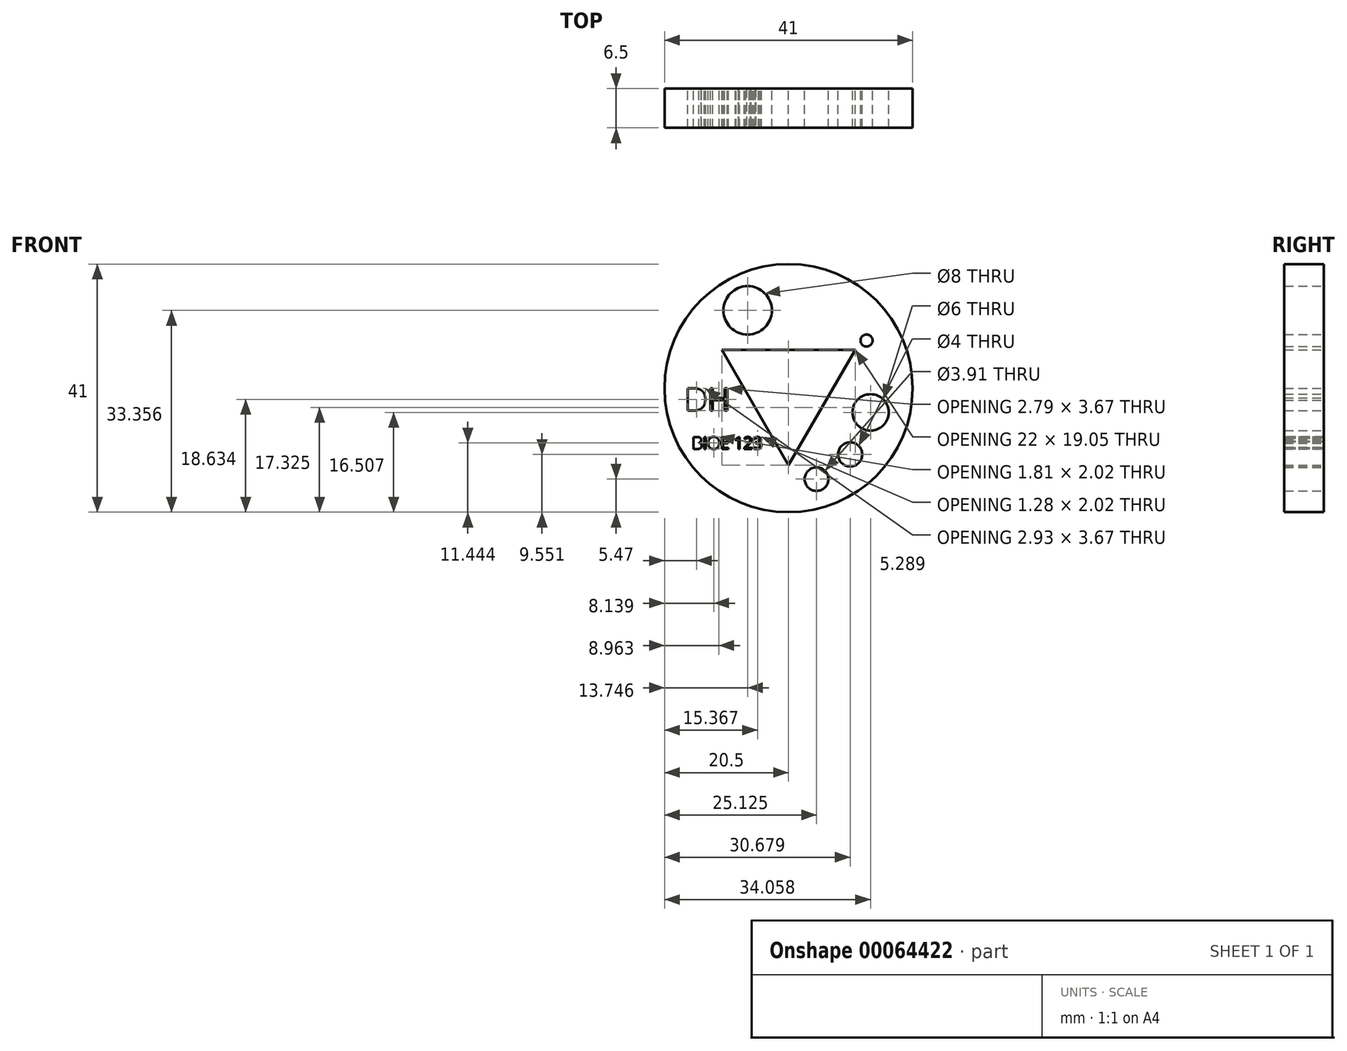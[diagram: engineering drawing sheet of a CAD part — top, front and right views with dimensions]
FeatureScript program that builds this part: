
annotation { "Feature Type Name" : "Feature", "Feature Type Description" : "" }
export const myFeature = defineFeature(function(context is Context, id is Id, definition is map)
    precondition{}
    {
        {
            var Q0;
            Q0=qCreatedBy(makeId("Front.planeOp"),FACE);
            var sketch = newSketch(context, id + "F0", { "sketchPlane" : qUnion([Q0])});
            skCircle(sketch, "E0", {"center": v(0, 0) * mm, "radius": 27.5 * mm});
            skCircle(sketch, "E1", {"center": v(0, 0) * mm, "radius": 20.5 * mm});
            skCircle(sketch, "E2", {"center": v(-6.75, 12.86) * mm, "radius": 4 * mm});
            skCircle(sketch, "E3", {"center": v(13.56, -4) * mm, "radius": 3 * mm});
            skCircle(sketch, "E4", {"center": v(10.18, -10.95) * mm, "radius": 2 * mm});
            skCircle(sketch, "E5", {"center": v(4.62, -15.03) * mm, "radius": 1.96 * mm});
            skCircle(sketch, "E6", {"center": v(12.89, 7.88) * mm, "radius": 1 * mm});
            skText(sketch, "E7", { "text": "DH", "fontName": "OpenSans-Regular.ttf"});
            skLineSegment(sketch, "E8.0", {"start": v(0, -12.7) * mm, "end": v(-11, 6.35) * mm});
            skLineSegment(sketch, "E8.1", {"start": v(-11, 6.35) * mm, "end": v(11, 6.35) * mm});
            skLineSegment(sketch, "E8.2", {"start": v(11, 6.35) * mm, "end": v(0, -12.7) * mm});
            skLineSegment(sketch, "E9", {"start": v(0, 4.63) * mm, "end": v(-4.13, -2.53) * mm});
            skLineSegment(sketch, "E10", {"start": v(-4.13, -2.53) * mm, "end": v(4.13, -2.53) * mm});
            skLineSegment(sketch, "E11", {"start": v(0, 4.63) * mm, "end": v(4.13, -2.53) * mm});
            skText(sketch, "E12", { "text": "BIOE 123\n", "fontName": "OpenSans-Regular.ttf"});
            const initialGuessF0  = {"E7": [-0.01718, -0.0037, 1, 0, 0.0037], "E12": [-0.01598, -0.01004, 1, 0, 0.00198]};
            skSetInitialGuess(sketch, initialGuessF0);
            skSolve(sketch);
        }
        {
            var Q0;
            Q0=makeQuery(id+"F0.imprint","IMPRINT",FACE,{"disambiguationData":[TD([[makeQuery(id+"F0.imprint","IMPRINT",EDGE,{"derivedFrom":sQuery(id+"F0.wireOp",EDGE,"E1")}),1.0]])]});
            extrude(context, id + "F1", {"entities" : qUnion([Q0]), "depth" : 6.5 * mm});
        }
    });
